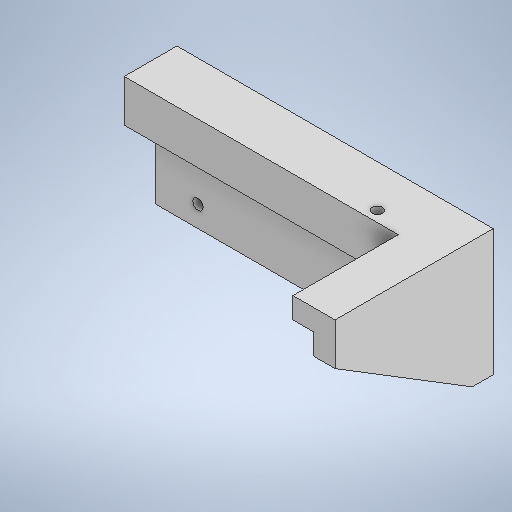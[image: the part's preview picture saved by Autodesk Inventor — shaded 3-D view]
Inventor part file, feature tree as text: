
AUTODESK INVENTOR PART (.ipt)
format: ipt  version: 2025.3 (Build 293356000, 356)  size: 291,840 bytes
history: native  units: mm
features: extrude x6, sketch x5, other x3, projected_geometry x2, mirror x1, hole x1
ambient origin geometry x8: Origin, YZ Plane, XZ Plane, XY Plane, X Axis, Y Axis, Z Axis, Center Point
bodies: Body1 (feature_tree)
feature tree (18):
  other  "솔리드1"
  sketch  "스케치1"
  extrude  "돌출1"  Depth=10.0mm
  extrude  "돌출2"  Depth=300.0mm
  extrude  "돌출3"  Depth=25.0mm TaperAngle=0.0deg
  extrude  "돌출4"  Depth=60.0mm
  other  "작업 평면1"
  mirror  "미러1"
  extrude  "돌출5"  Depth=10.0mm TaperAngle=0.0deg
  hole  "구멍1"  [1 undecoded]
  other  "작업 평면2"
  extrude  "돌출6"  Depth=10.0mm
  sketch  "스케치2"
  projected_geometry  "투영된 루프1"
  sketch  "스케치3"
  sketch  "스케치4"
  sketch  "스케치5"
  projected_geometry  "투영된 루프2"
note: 1 required parameter value undecoded (feature->parameter linkage not recoverable at this tier; creation-order binding heuristic only, values carry confidence <= 0.55)
